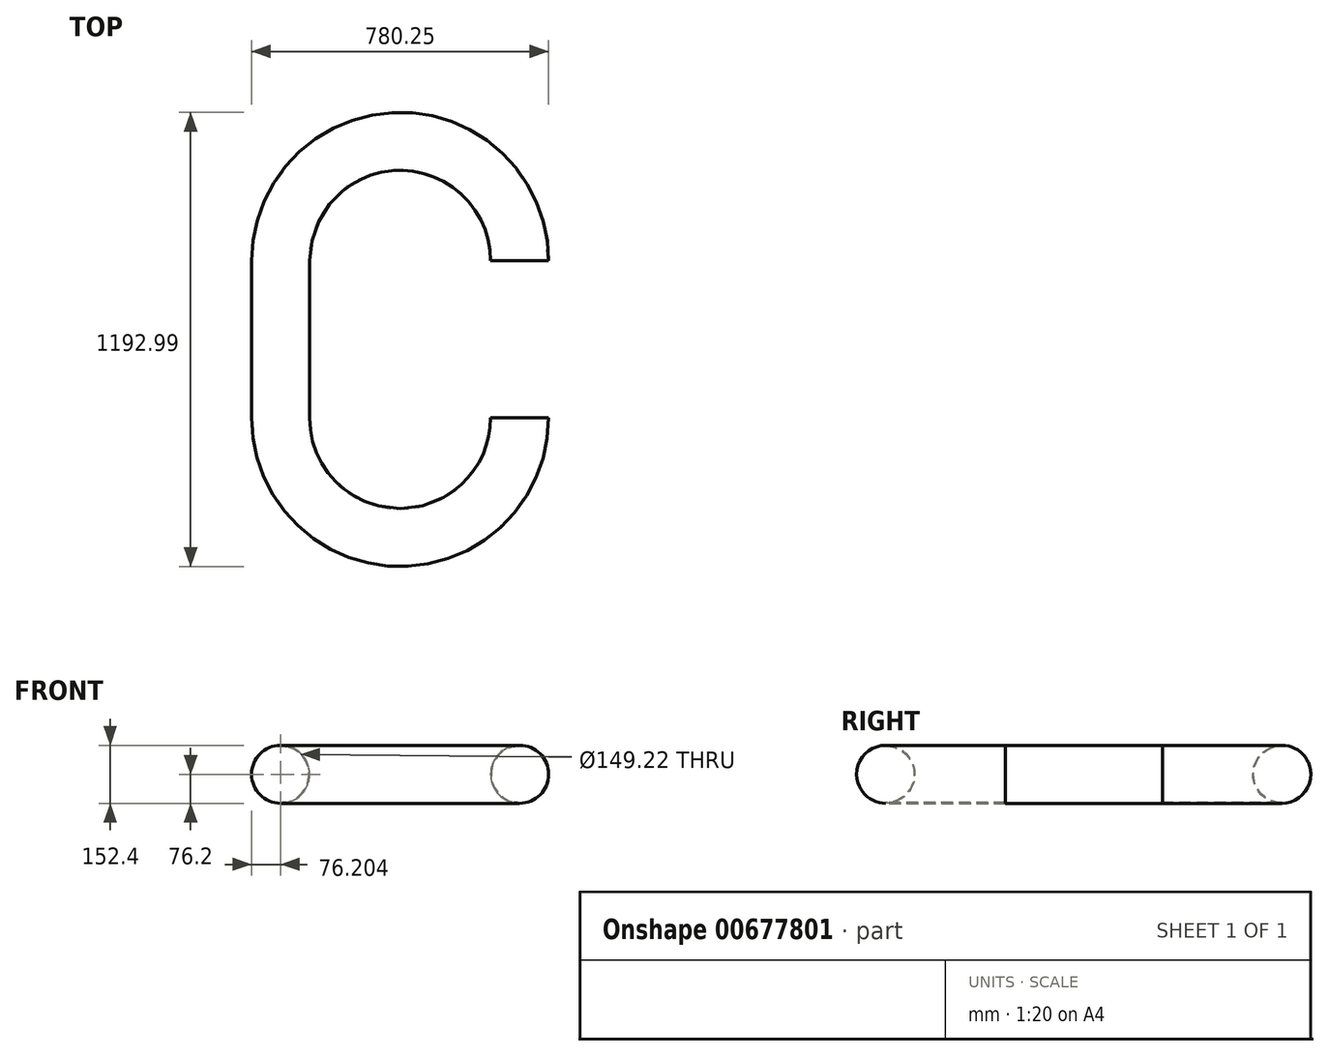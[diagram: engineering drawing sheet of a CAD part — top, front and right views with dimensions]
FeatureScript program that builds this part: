
annotation { "Feature Type Name" : "Feature", "Feature Type Description" : "" }
export const myFeature = defineFeature(function(context is Context, id is Id, definition is map)
    precondition{}
    {
        {
            var Q0;
            Q0=qCreatedBy(makeId("Front.planeOp"),FACE);
            var sketch = newSketch(context, id + "F0", { "sketchPlane" : qUnion([Q0])});
            skCircle(sketch, "E0", {"center": v(0, 0) * mm, "radius": 74.61 * mm});
            skCircle(sketch, "E1", {"center": v(0, 0) * mm, "radius": 76.2 * mm});
            skSolve(sketch);
        }
        {
            var Q0;
            Q0=qCreatedBy(makeId("Top.planeOp"),FACE);
            var sketch = newSketch(context, id + "F1", { "sketchPlane" : qUnion([Q0])});
            skLineSegment(sketch, "E2", {"start": v(-76.2, 0) * mm, "end": v(-76.2, 412.75) * mm});
            skLineSegment(sketch, "E3", {"start": v(-39.08, 0) * mm, "end": v(-551.65, 0) * mm, "construction": true});
            skLineSegment(sketch, "E4", {"start": v(-551.65, 0) * mm, "end": v(-551.65, 412.75) * mm});
            skArc(sketch, "E5", {"start": v(-76.2, 412.75) * mm, "mid": v(-313.92, 650.47) * mm, "end": v(-551.65, 412.75) * mm});
            skPoint(sketch, "E5.third.point", {"position": v(-310.03, 175.06) * mm});
            skArc(sketch, "E6", {"start": v(-551.65, 0) * mm, "mid": v(-313.92, -237.72) * mm, "end": v(-76.2, 0) * mm});
            skPoint(sketch, "E6.third.point", {"position": v(-492.06, -157.42) * mm});
            skSolve(sketch);
        }
        {
            var Q0;
            Q0=makeQuery(id+"F0.imprint","IMPRINT",FACE,{"disambiguationData":[TD([[makeQuery(id+"F0.imprint","IMPRINT",EDGE,{"derivedFrom":sQuery(id+"F0.wireOp",EDGE,"E0")}),-1.0]])]});
            var Q1;
            Q1=sQuery(id+"F1.wireOp",EDGE,"E5");
            var Q2;
            Q2=sQuery(id+"F1.wireOp",EDGE,"E4");
            var Q3;
            Q3=sQuery(id+"F1.wireOp",EDGE,"E6");
            sweep(context, id + "F2", {"profiles" : qUnion([Q0]), "path" : qUnion([Q1, Q2, Q3])});
        }
    });
